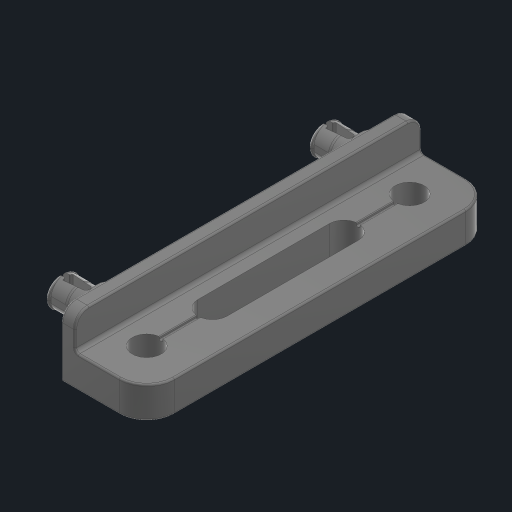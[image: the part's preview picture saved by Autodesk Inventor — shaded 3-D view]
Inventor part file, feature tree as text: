
AUTODESK INVENTOR PART (.ipt)
format: ipt  version: 2023 (Build 270158030, 158C)  size: 688,640 bytes
history: native  units: in
note: dims shown in document units (in); Inventor stores cm internally (conversion verified against a paired STEP export)
features: fillet x1
ambient origin geometry x8: Origin, YZ Plane, XZ Plane, XY Plane, X Axis, Y Axis, Z Axis, Center Point
bodies: Solid1 (feature_tree)
feature tree (1):
  fillet  "Fillet7"  [1 undecoded]
note: 1 required parameter value undecoded (feature->parameter linkage not recoverable at this tier; creation-order binding heuristic only, values carry confidence <= 0.55)
